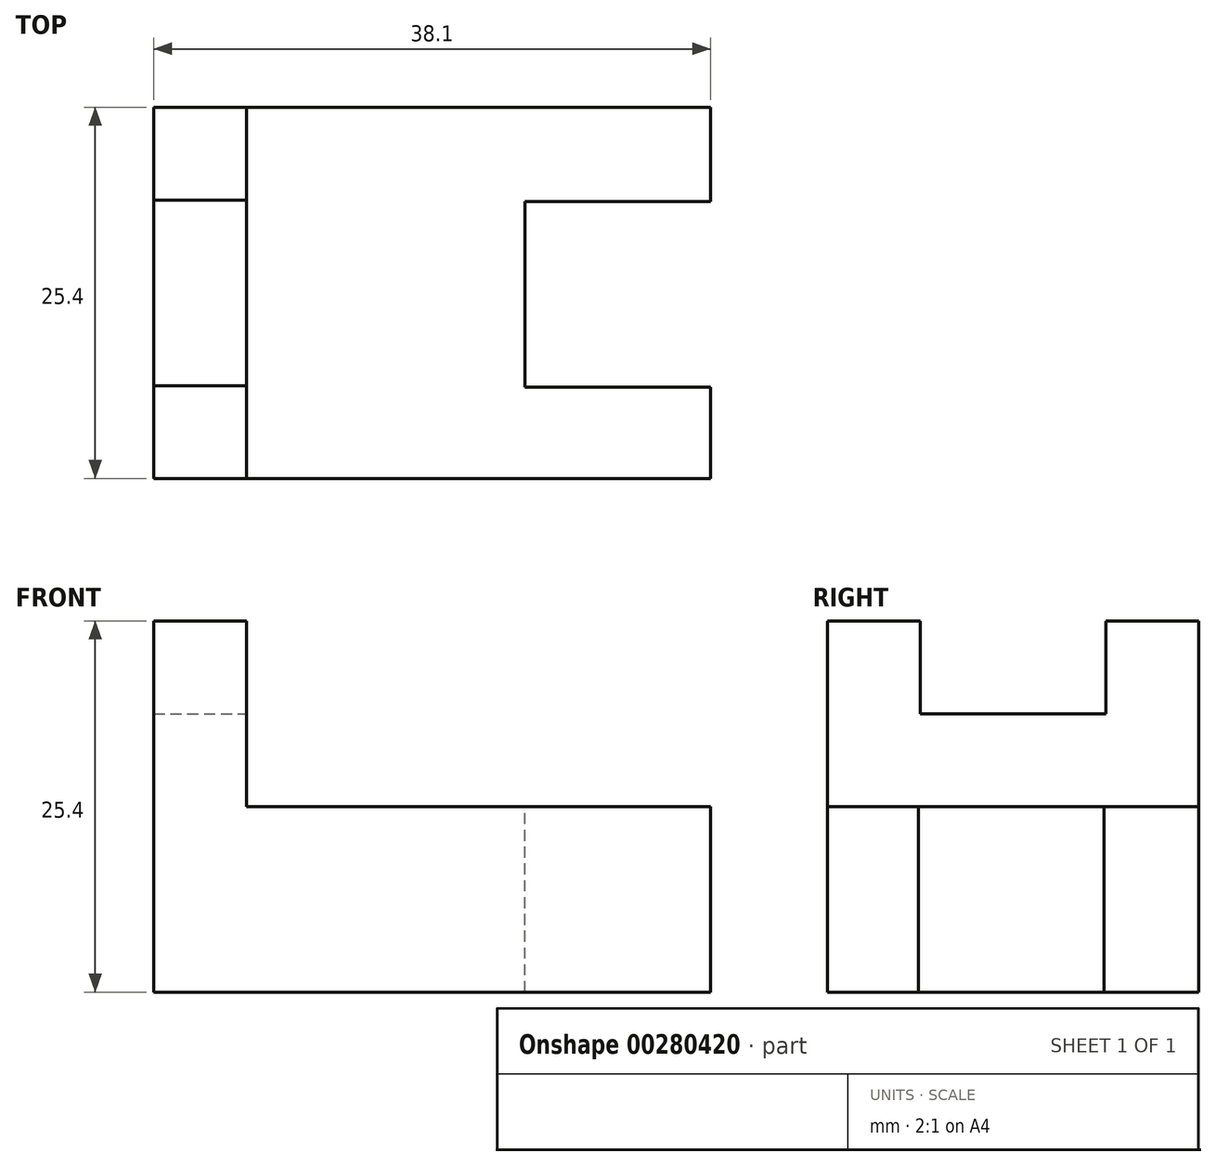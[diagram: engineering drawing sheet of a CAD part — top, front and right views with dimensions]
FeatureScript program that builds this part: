
annotation { "Feature Type Name" : "Feature", "Feature Type Description" : "" }
export const myFeature = defineFeature(function(context is Context, id is Id, definition is map)
    precondition{}
    {
        {
            var Q0;
            Q0=qCreatedBy(makeId("Front.planeOp"),FACE);
            var sketch = newSketch(context, id + "F0", { "sketchPlane" : qUnion([Q0])});
            skLineSegment(sketch, "E0.bottom", {"start": v(0, 0) * mm, "end": v(38.1, 0) * mm});
            skLineSegment(sketch, "E0.top", {"start": v(0, 25.4) * mm, "end": v(38.1, 25.4) * mm});
            skLineSegment(sketch, "E0.left", {"start": v(0, 0) * mm, "end": v(0, 25.4) * mm});
            skLineSegment(sketch, "E0.right", {"start": v(38.1, 0) * mm, "end": v(38.1, 25.4) * mm});
            skSolve(sketch);
        }
        {
            var Q0;
            Q0 = qSketchRegion(id + "F0", true);
            extrude(context, id + "F1", {"entities" : qUnion([Q0]), "depth" : 25.4 * mm, "symmetric" : true});
        }
        {
            var Q0;
            Q0=makeQuery(id+"F1.opExtrude","CAP_FACE",FACE,{"disambiguationData":[OSD([sQuery(id+"F0.wireOp",EDGE,"E0.bottom"),sQuery(id+"F0.wireOp",EDGE,"E0.top"),sQuery(id+"F0.wireOp",EDGE,"E0.left"),sQuery(id+"F0.wireOp",EDGE,"E0.right")])],"isStart":false});
            var sketch = newSketch(context, id + "F2", { "sketchPlane" : qUnion([Q0])});
            skLineSegment(sketch, "E1", {"start": v(38.1, 25.4) * mm, "end": v(6.35, 25.4) * mm});
            skLineSegment(sketch, "E2", {"start": v(6.35, 25.4) * mm, "end": v(6.35, 12.7) * mm});
            skPoint(sketch, "E2.endSnap0", {"position": v(0, 12.7) * mm});
            skLineSegment(sketch, "E3", {"start": v(6.35, 12.7) * mm, "end": v(38.1, 12.7) * mm});
            skLineSegment(sketch, "E4", {"start": v(38.1, 12.7) * mm, "end": v(38.1, 25.4) * mm});
            skSolve(sketch);
        }
        {
            var Q0;
            Q0=makeQuery(id+"F2.imprint","IMPRINT",FACE,{"disambiguationData":[TD([[makeQuery(id+"F2.imprint","IMPRINT",EDGE,{"derivedFrom":sQuery(id+"F2.wireOp",EDGE,"E1")}),-1.0]])]});
            extrude(context, id + "F3", {"entities" : qUnion([Q0]), "operationType" : NewBodyOperationType.REMOVE, "endBound" : BoundingType.THROUGH_ALL, "oppositeDirection" : true, "depth" : 25.4 * mm});
        }
        {
            var Q0;
            Q0=makeQuery(id+"F3.boolean.opBoolean","COPY",FACE,{"derivedFrom":makeQuery(id+"F3.opExtrude","SWEPT_FACE",FACE,{"disambiguationData":[OSD([sQuery(id+"F2.wireOp",EDGE,"E3")])]})});
            var sketch = newSketch(context, id + "F4", { "sketchPlane" : qUnion([Q0])});
            skLineSegment(sketch, "E5", {"start": v(38.1, 0) * mm, "end": v(38.1, -6.46) * mm});
            skLineSegment(sketch, "E6", {"start": v(38.1, -6.46) * mm, "end": v(25.4, -6.46) * mm});
            skLineSegment(sketch, "E7", {"start": v(25.4, -6.46) * mm, "end": v(25.4, 6.24) * mm});
            skLineSegment(sketch, "E8", {"start": v(25.4, 6.24) * mm, "end": v(38.1, 6.24) * mm});
            skLineSegment(sketch, "E9", {"start": v(38.1, 0) * mm, "end": v(38.1, 6.24) * mm});
            skSolve(sketch);
        }
        {
            var Q0;
            Q0 = qSketchRegion(id + "F4", true);
            extrude(context, id + "F5", {"entities" : qUnion([Q0]), "operationType" : NewBodyOperationType.REMOVE, "endBound" : BoundingType.THROUGH_ALL, "oppositeDirection" : true, "depth" : 25.4 * mm});
        }
        {
            var Q0;
            Q0=makeQuery(id+"F1.opExtrude","SWEPT_FACE",FACE,{"disambiguationData":[OSD([sQuery(id+"F0.wireOp",EDGE,"E0.top")])]});
            var sketch = newSketch(context, id + "F6", { "sketchPlane" : qUnion([Q0])});
            skLineSegment(sketch, "E10", {"start": v(0, 0) * mm, "end": v(0, 6.33) * mm});
            skLineSegment(sketch, "E11", {"start": v(0, 6.33) * mm, "end": v(6.35, 6.33) * mm});
            skLineSegment(sketch, "E12", {"start": v(6.35, 6.33) * mm, "end": v(6.35, -6.37) * mm});
            skLineSegment(sketch, "E13", {"start": v(6.35, -6.37) * mm, "end": v(0, -6.37) * mm});
            skLineSegment(sketch, "E14", {"start": v(0, -6.37) * mm, "end": v(0, 6.33) * mm});
            skSolve(sketch);
        }
        {
            var Q0;
            Q0 = qSketchRegion(id + "F6", true);
            extrude(context, id + "F7", {"entities" : qUnion([Q0]), "operationType" : NewBodyOperationType.REMOVE, "oppositeDirection" : true, "depth" : 6.35 * mm});
        }
    });
